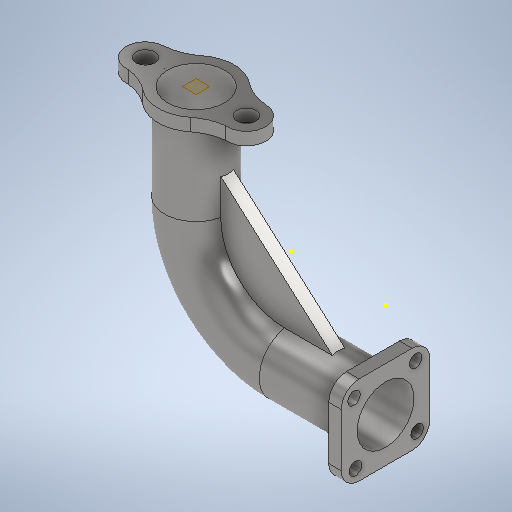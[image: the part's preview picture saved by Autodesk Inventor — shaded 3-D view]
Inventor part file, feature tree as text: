
AUTODESK INVENTOR PART (.ipt)
format: ipt  version: 2025.2 (Build 292293000, 293)  size: 489,472 bytes
history: native  units: in
note: dims shown in document units (in); Inventor stores cm internally (conversion verified against a paired STEP export)
features: sketch x9, extrude x3, plane x1, sweep x1, rib x1
ambient origin geometry x8: Origin, YZ Plane, XZ Plane, XY Plane, X Axis, Y Axis, Z Axis, Center Point
bodies: Solid1 (feature_tree)
feature tree (15):
  sketch  "Sketch1"  dims[d4=3.937in d5=3.5433in]
  sketch  "Sketch2"  dims[d9=2.3622in d11=1.1811in]
  plane  "Work Plane1"
  sweep  "Sweep1"
  extrude  "Extrusion1"  Depth=4.7244in
  extrude  "Extrusion2"  Depth=1.1811in
  sketch  "Sketch6"  dims[d18=5.5118in]
  extrude  "Extrusion3"  Depth=3.1496in
  rib  "Rib1"
  sketch  "Sketch3"  dims[d13=3.1496in d14=3.5433in]
  sketch  "Sketch4"  dims[d15=0.7874in d16=0.0in]
  sketch  "Sketch5"  dims[d17=5.5118in]
  sketch  "Sketch7"  dims[d19=1.1024in]
  sketch  "Sketch Circular Pattern1"  dims[d6=0.0in d7=0.0in d8=4.7244in]
  sketch  "Sketch8"  dims[d20=3.5433in d21=0.7874in d22=0.0in d23=0.7874in d24=3.5433in d25=1.5748in d27=360.0deg d29=0.7874in d30=0.0in d32=0.0394in d33=0.7874in d34=0.0in d35=0.0in d36=0.0394in d37=0.0394in]
